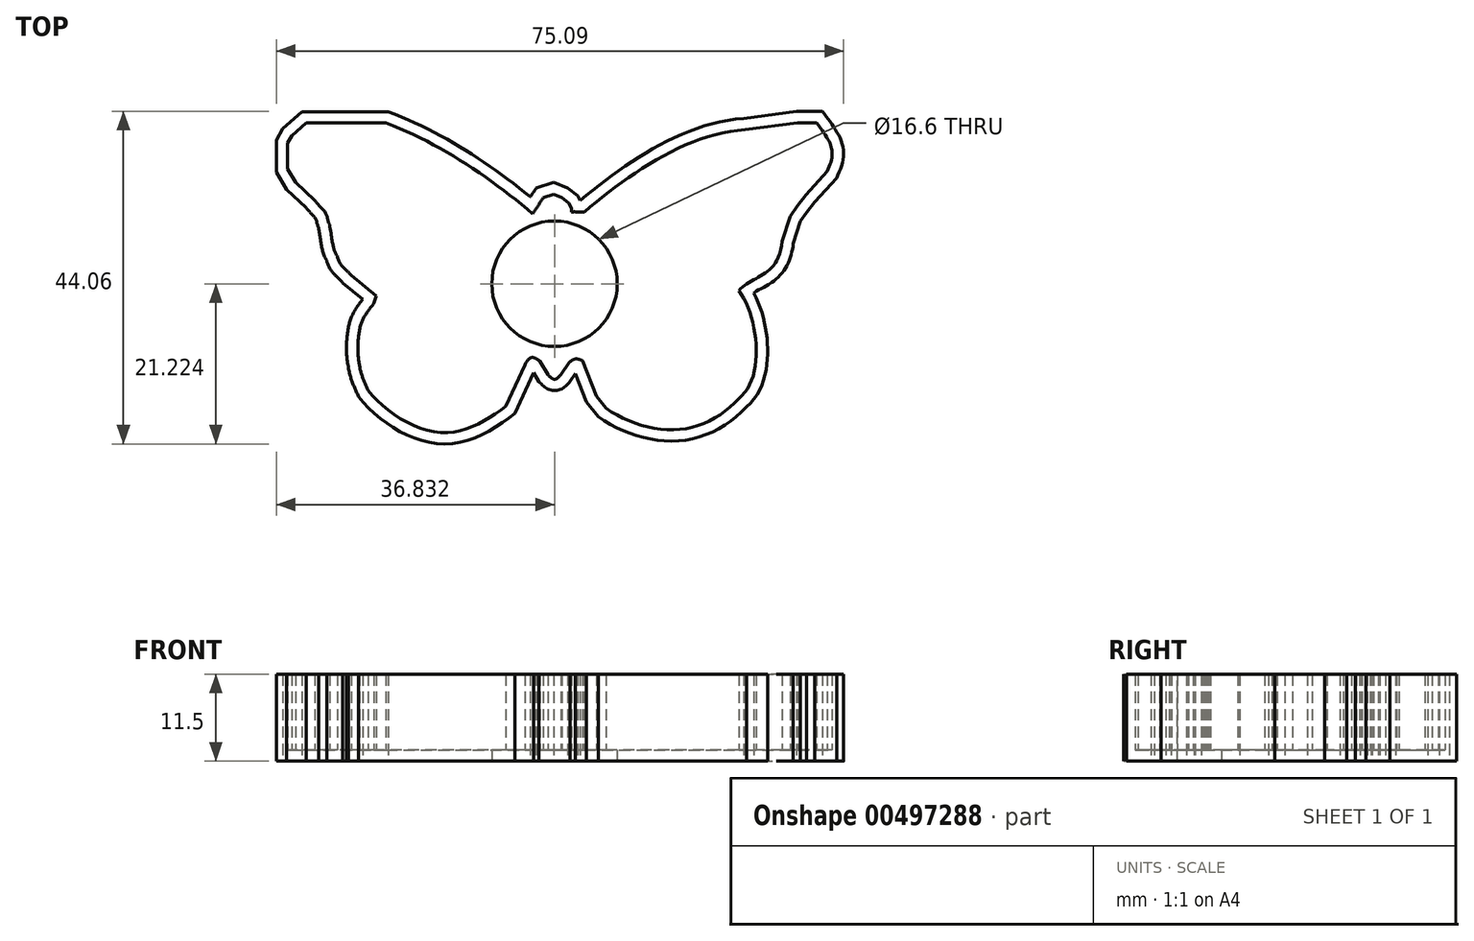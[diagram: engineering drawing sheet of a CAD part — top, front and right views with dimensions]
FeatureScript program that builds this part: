
annotation { "Feature Type Name" : "Feature", "Feature Type Description" : "" }
export const myFeature = defineFeature(function(context is Context, id is Id, definition is map)
    precondition{}
    {
        {
            var Q0;
            Q0=qCreatedBy(makeId("Top.planeOp"),FACE);
            var sketch = newSketch(context, id + "F0", { "sketchPlane" : qUnion([Q0])});
            skLineSegment(sketch, "E0", {"start": v(4.53, 23.83) * mm, "end": v(15.09, 23.83) * mm});
            skFitSpline(sketch, "E1", {"points": [v(15.09, 23.83) * mm, v(34.52, 11.81) * mm], "startDerivative": vector(20.93, -7.78) * mm, "endDerivative": vector(16.93, -14.37) * mm});
            skFitSpline(sketch, "E2", {"points": [v(34.52, 11.81) * mm, v(35.9, 13.93) * mm], "startDerivative": vector(1.48, 2.12) * mm, "endDerivative": vector(1.48, 2.12) * mm});
            skFitSpline(sketch, "E3", {"points": [v(35.9, 13.93) * mm, v(37.27, 14.36) * mm], "startDerivative": vector(1.36, 0.44) * mm, "endDerivative": vector(1.36, 0.44) * mm});
            skFitSpline(sketch, "E4", {"points": [v(37.27, 14.36) * mm, v(38.38, 13.93) * mm], "startDerivative": vector(1.11, -0.44) * mm, "endDerivative": vector(1.11, -0.44) * mm});
            skFitSpline(sketch, "E5", {"points": [v(38.38, 13.93) * mm, v(39.27, 13.22) * mm], "startDerivative": vector(0.9, -0.7) * mm, "endDerivative": vector(0.9, -0.7) * mm});
            skFitSpline(sketch, "E6", {"points": [v(39.27, 13.22) * mm, v(39.63, 12.54) * mm], "startDerivative": vector(0.36, -0.68) * mm, "endDerivative": vector(0.36, -0.68) * mm});
            skFitSpline(sketch, "E7", {"points": [v(39.63, 12.54) * mm, v(39.63, 12.05) * mm], "startDerivative": vector(0, -0.5) * mm, "endDerivative": vector(0, -0.5) * mm});
            skFitSpline(sketch, "E8", {"points": [v(39.63, 12.05) * mm, v(40.16, 12.05) * mm], "startDerivative": vector(0.53, -0.4) * mm, "endDerivative": vector(0.53, -0.4) * mm});
            skFitSpline(sketch, "E9", {"points": [v(40.16, 12.05) * mm, v(41.35, 12.05) * mm], "startDerivative": vector(0.5, 0) * mm, "endDerivative": vector(0.5, 0) * mm});
            skFitSpline(sketch, "E10", {"points": [v(41.35, 12.05) * mm, v(62.6, 22.94) * mm], "startDerivative": vector(17.5, 15.04) * mm, "endDerivative": vector(22.58, 1.26) * mm});
            skLineSegment(sketch, "E11", {"start": v(62.6, 22.94) * mm, "end": v(69.55, 23.88) * mm});
            skFitSpline(sketch, "E12", {"points": [v(69.55, 23.88) * mm, v(72.1, 23.88) * mm], "startDerivative": vector(2.54, 0) * mm, "endDerivative": vector(2.54, 0) * mm});
            skFitSpline(sketch, "E13", {"points": [v(72.1, 23.88) * mm, v(73.47, 17.41) * mm], "startDerivative": vector(6.36, -8.58) * mm, "endDerivative": vector(-3.81, -7.95) * mm});
            skFitSpline(sketch, "E14", {"points": [v(73.47, 17.41) * mm, v(70.71, 14.34) * mm], "startDerivative": vector(-2.75, -3.07) * mm, "endDerivative": vector(-2.75, -3.07) * mm});
            skFitSpline(sketch, "E15", {"points": [v(70.71, 14.34) * mm, v(69.55, 12.86) * mm], "startDerivative": vector(-1.17, -1.48) * mm, "endDerivative": vector(-1.17, -1.48) * mm});
            skFitSpline(sketch, "E16", {"points": [v(69.55, 12.86) * mm, v(68.6, 11.48) * mm], "startDerivative": vector(-0.95, -1.38) * mm, "endDerivative": vector(-0.95, -1.38) * mm});
            skFitSpline(sketch, "E17", {"points": [v(68.6, 11.48) * mm, v(67.54, 8.2) * mm], "startDerivative": vector(-1.06, -3.28) * mm, "endDerivative": vector(-1.06, -3.28) * mm});
            skFitSpline(sketch, "E18", {"points": [v(67.54, 8.2) * mm, v(61.78, 1.6) * mm], "startDerivative": vector(-1.59, -14.94) * mm, "endDerivative": vector(-5.4, -6.57) * mm});
            skFitSpline(sketch, "E19", {"points": [v(61.78, 1.6) * mm, v(61.78, -12.65) * mm], "startDerivative": vector(8.1, -10.54) * mm, "endDerivative": vector(-10.46, -7.95) * mm});
            skFitSpline(sketch, "E20", {"points": [v(61.78, -12.65) * mm, v(53.85, -16.77) * mm, v(44.22, -13.95) * mm], "startDerivative": vector(-12.8, -14.02) * mm, "endDerivative": vector(-15.73, 11.03) * mm});
            skFitSpline(sketch, "E21", {"points": [v(44.22, -13.95) * mm, v(42.95, -12.36) * mm], "startDerivative": vector(-1.27, 1.59) * mm, "endDerivative": vector(-1.27, 1.59) * mm});
            skLineSegment(sketch, "E22", {"start": v(42.95, -12.36) * mm, "end": v(41.09, -7.65) * mm});
            skFitSpline(sketch, "E23", {"points": [v(41.09, -7.65) * mm, v(39.3, -7.9) * mm], "startDerivative": vector(-1.78, 0.91) * mm, "endDerivative": vector(-1.97, -1.98) * mm});
            skLineSegment(sketch, "E24", {"start": v(39.3, -7.9) * mm, "end": v(38.24, -9.49) * mm});
            skFitSpline(sketch, "E25", {"points": [v(38.24, -9.49) * mm, v(36.52, -9.49) * mm], "startDerivative": vector(-2.36, -3.03) * mm, "endDerivative": vector(-1.91, 1.91) * mm});
            skLineSegment(sketch, "E26", {"start": v(36.52, -9.49) * mm, "end": v(35.47, -7.69) * mm});
            skFitSpline(sketch, "E27", {"points": [v(35.47, -7.69) * mm, v(33.48, -8.21) * mm], "startDerivative": vector(-2.14, 1.57) * mm, "endDerivative": vector(-1.8, -4.27) * mm});
            skLineSegment(sketch, "E28", {"start": v(33.48, -8.21) * mm, "end": v(30.97, -13.68) * mm});
            skFitSpline(sketch, "E29", {"points": [v(30.97, -13.68) * mm, v(22.34, -17.17) * mm, v(12.74, -11.6) * mm], "startDerivative": vector(-15.72, -11.63) * mm, "endDerivative": vector(-11.84, 15.5) * mm});
            skFitSpline(sketch, "E30", {"points": [v(12.74, -11.6) * mm, v(11.58, -8.14) * mm], "startDerivative": vector(-1.55, 3.4) * mm, "endDerivative": vector(-0.34, 3.7) * mm});
            skFitSpline(sketch, "E31", {"points": [v(11.58, -8.14) * mm, v(11.58, -3.6) * mm], "startDerivative": vector(-0.93, 3.88) * mm, "endDerivative": vector(0.76, 3.96) * mm});
            skFitSpline(sketch, "E32", {"points": [v(11.58, -3.6) * mm, v(13.5, 0) * mm], "startDerivative": vector(0.76, 4.65) * mm, "endDerivative": vector(2.7, 3.74) * mm});
            skFitSpline(sketch, "E33", {"points": [v(13.5, 0) * mm, v(13.8, 0.93) * mm], "startDerivative": vector(0.3, 0.93) * mm, "endDerivative": vector(0.3, 0.93) * mm});
            skFitSpline(sketch, "E34", {"points": [v(13.8, 0.93) * mm, v(10.47, 3.66) * mm], "startDerivative": vector(-3.33, 2.73) * mm, "endDerivative": vector(-3.33, 2.73) * mm});
            skFitSpline(sketch, "E35", {"points": [v(10.47, 3.66) * mm, v(8.62, 6.26) * mm], "startDerivative": vector(-1.78, 2.53) * mm, "endDerivative": vector(-0.95, 4.54) * mm});
            skFitSpline(sketch, "E36", {"points": [v(8.62, 6.26) * mm, v(7.61, 10.41) * mm], "startDerivative": vector(-1.7, 2.08) * mm, "endDerivative": vector(-1.32, 7.56) * mm});
            skFitSpline(sketch, "E37", {"points": [v(7.61, 10.41) * mm, v(7.13, 11.84) * mm, v(5.68, 13.58) * mm], "startDerivative": vector(-1.93, 3.16) * mm, "endDerivative": vector(-1.93, 3.16) * mm});
            skFitSpline(sketch, "E38", {"points": [v(5.68, 13.58) * mm, v(3.13, 15.97) * mm], "startDerivative": vector(-2.55, 2.4) * mm, "endDerivative": vector(-2.55, 2.4) * mm});
            skFitSpline(sketch, "E39", {"points": [v(3.13, 15.97) * mm, v(2.06, 17.73) * mm], "startDerivative": vector(-1.07, 1.76) * mm, "endDerivative": vector(-1.07, 1.76) * mm});
            skFitSpline(sketch, "E40", {"points": [v(2.06, 17.73) * mm, v(2.06, 19.78) * mm], "startDerivative": vector(0, 2.05) * mm, "endDerivative": vector(0, 2.05) * mm});
            skFitSpline(sketch, "E41", {"points": [v(2.06, 19.78) * mm, v(2.06, 21.17) * mm], "startDerivative": vector(0, 1.39) * mm, "endDerivative": vector(0, 1.39) * mm});
            skFitSpline(sketch, "E42", {"points": [v(2.06, 21.17) * mm, v(2.62, 22.15) * mm], "startDerivative": vector(0.56, 0.98) * mm, "endDerivative": vector(0.56, 0.98) * mm});
            skFitSpline(sketch, "E43", {"points": [v(2.62, 22.15) * mm, v(4.53, 23.83) * mm], "startDerivative": vector(1.91, 1.68) * mm, "endDerivative": vector(1.91, 1.68) * mm});
            skSolve(sketch);
        }
        {
            var Q0;
            Q0=makeQuery(id+"F0.imprint","IMPRINT",FACE,{"disambiguationData":[TD([[makeQuery(id+"F0.imprint","IMPRINT",EDGE,{"derivedFrom":sQuery(id+"F0.wireOp",EDGE,"E0")}),-1.0]])]});
            extrude(context, id + "F1", {"entities" : qUnion([Q0]), "depth" : 10 * mm});
        }
        {
            var Q0;
            Q0=makeQuery(id+"F1.opExtrude","CAP_FACE",FACE,{"disambiguationData":[OSD([sQuery(id+"F0.wireOp",EDGE,"E0"),sQuery(id+"F0.wireOp",EDGE,"E1"),sQuery(id+"F0.wireOp",EDGE,"E2"),sQuery(id+"F0.wireOp",EDGE,"E3"),sQuery(id+"F0.wireOp",EDGE,"E4"),sQuery(id+"F0.wireOp",EDGE,"E5"),sQuery(id+"F0.wireOp",EDGE,"E6"),sQuery(id+"F0.wireOp",EDGE,"E7"),sQuery(id+"F0.wireOp",EDGE,"E8"),sQuery(id+"F0.wireOp",EDGE,"E9"),sQuery(id+"F0.wireOp",EDGE,"E10"),sQuery(id+"F0.wireOp",EDGE,"E11"),sQuery(id+"F0.wireOp",EDGE,"E12"),sQuery(id+"F0.wireOp",EDGE,"E13"),sQuery(id+"F0.wireOp",EDGE,"E14"),sQuery(id+"F0.wireOp",EDGE,"E15"),sQuery(id+"F0.wireOp",EDGE,"E16"),sQuery(id+"F0.wireOp",EDGE,"E17"),sQuery(id+"F0.wireOp",EDGE,"E18"),sQuery(id+"F0.wireOp",EDGE,"E19"),sQuery(id+"F0.wireOp",EDGE,"E20"),sQuery(id+"F0.wireOp",EDGE,"E21"),sQuery(id+"F0.wireOp",EDGE,"E22"),sQuery(id+"F0.wireOp",EDGE,"E23"),sQuery(id+"F0.wireOp",EDGE,"E24"),sQuery(id+"F0.wireOp",EDGE,"E25"),sQuery(id+"F0.wireOp",EDGE,"E26"),sQuery(id+"F0.wireOp",EDGE,"E27"),sQuery(id+"F0.wireOp",EDGE,"E28"),sQuery(id+"F0.wireOp",EDGE,"E29"),sQuery(id+"F0.wireOp",EDGE,"E30"),sQuery(id+"F0.wireOp",EDGE,"E31"),sQuery(id+"F0.wireOp",EDGE,"E32"),sQuery(id+"F0.wireOp",EDGE,"E33"),sQuery(id+"F0.wireOp",EDGE,"E34"),sQuery(id+"F0.wireOp",EDGE,"E35"),sQuery(id+"F0.wireOp",EDGE,"E36"),sQuery(id+"F0.wireOp",EDGE,"E37"),sQuery(id+"F0.wireOp",EDGE,"E38"),sQuery(id+"F0.wireOp",EDGE,"E39"),sQuery(id+"F0.wireOp",EDGE,"E40"),sQuery(id+"F0.wireOp",EDGE,"E41"),sQuery(id+"F0.wireOp",EDGE,"E42"),sQuery(id+"F0.wireOp",EDGE,"E43")])],"isStart":false});
            shell(context, id + "F2", {"entities" : qUnion([Q0]), "thickness" : 1.5 * mm, "oppositeDirection" : true});
        }
        {
            var Q0;
            Q0=makeQuery(id+"F1.opExtrude","CAP_FACE",FACE,{"disambiguationData":[OSD([sQuery(id+"F0.wireOp",EDGE,"E0"),sQuery(id+"F0.wireOp",EDGE,"E1"),sQuery(id+"F0.wireOp",EDGE,"E2"),sQuery(id+"F0.wireOp",EDGE,"E3"),sQuery(id+"F0.wireOp",EDGE,"E4"),sQuery(id+"F0.wireOp",EDGE,"E5"),sQuery(id+"F0.wireOp",EDGE,"E6"),sQuery(id+"F0.wireOp",EDGE,"E7"),sQuery(id+"F0.wireOp",EDGE,"E8"),sQuery(id+"F0.wireOp",EDGE,"E9"),sQuery(id+"F0.wireOp",EDGE,"E10"),sQuery(id+"F0.wireOp",EDGE,"E11"),sQuery(id+"F0.wireOp",EDGE,"E12"),sQuery(id+"F0.wireOp",EDGE,"E13"),sQuery(id+"F0.wireOp",EDGE,"E14"),sQuery(id+"F0.wireOp",EDGE,"E15"),sQuery(id+"F0.wireOp",EDGE,"E16"),sQuery(id+"F0.wireOp",EDGE,"E17"),sQuery(id+"F0.wireOp",EDGE,"E18"),sQuery(id+"F0.wireOp",EDGE,"E19"),sQuery(id+"F0.wireOp",EDGE,"E20"),sQuery(id+"F0.wireOp",EDGE,"E21"),sQuery(id+"F0.wireOp",EDGE,"E22"),sQuery(id+"F0.wireOp",EDGE,"E23"),sQuery(id+"F0.wireOp",EDGE,"E24"),sQuery(id+"F0.wireOp",EDGE,"E25"),sQuery(id+"F0.wireOp",EDGE,"E26"),sQuery(id+"F0.wireOp",EDGE,"E27"),sQuery(id+"F0.wireOp",EDGE,"E28"),sQuery(id+"F0.wireOp",EDGE,"E29"),sQuery(id+"F0.wireOp",EDGE,"E30"),sQuery(id+"F0.wireOp",EDGE,"E31"),sQuery(id+"F0.wireOp",EDGE,"E32"),sQuery(id+"F0.wireOp",EDGE,"E33"),sQuery(id+"F0.wireOp",EDGE,"E34"),sQuery(id+"F0.wireOp",EDGE,"E35"),sQuery(id+"F0.wireOp",EDGE,"E36"),sQuery(id+"F0.wireOp",EDGE,"E37"),sQuery(id+"F0.wireOp",EDGE,"E38"),sQuery(id+"F0.wireOp",EDGE,"E39"),sQuery(id+"F0.wireOp",EDGE,"E40"),sQuery(id+"F0.wireOp",EDGE,"E41"),sQuery(id+"F0.wireOp",EDGE,"E42"),sQuery(id+"F0.wireOp",EDGE,"E43")])],"isStart":true});
            var sketch = newSketch(context, id + "F3", { "sketchPlane" : qUnion([Q0])});
            skCircle(sketch, "E44", {"center": v(37.4, -2.54) * mm, "radius": 8.3 * mm});
            skSolve(sketch);
        }
        {
            var Q0;
            Q0 = qSketchRegion(id + "F3", true);
            extrude(context, id + "F4", {"entities" : qUnion([Q0]), "operationType" : NewBodyOperationType.REMOVE, "oppositeDirection" : true, "depth" : 25.4 * mm});
        }
    });
